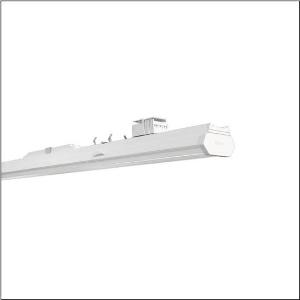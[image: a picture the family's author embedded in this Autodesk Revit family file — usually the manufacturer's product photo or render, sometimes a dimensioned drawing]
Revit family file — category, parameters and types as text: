
# Revit family: licross_r__21_protected_ho_52td12dn4e5md_1fe0
name_source: partatom
category: Lighting Fixtures
units: mm (PartAtom-declared; Revit-internal decimal feet)

## family parameters
Cut with Voids When Loaded = No
Host = Face
Light Source = No
Part Type = Normal
Room Calculation Point = No
Round Connector Dimension = Use Diameter
Shared = No

## types (1)
- --- (1 x LED, 2200 lm, 14.2 W, 4000K)
    Apparent Load = 14 VA
    CIE Flux Codes = 70 91 97 98 100
    Color Rendering = 80
    Color Temperature = 4000K
    Default Elevation = 1800 mm
    Description = Licross® 21 Protected HO, luminaire insert, of sheet steel, galvanised, coil coated, white, length: 1.500mm, width: 90mm, height: 103mm, LED rated luminous flux: 14.690lm, light colour: 840, control gear: DALI 2 (for two DALI lines), with plug, 6-pole, with phase selection, mains connection: 220..240V, AC/DC, 0/50..60Hz, rated input power: 85W, without changeover relay, for emergency light function, for central battery installations according to DIN EN 60598-2-22, halogen-free wiring, primary light control with lens, of plastic, primary optical cover: cover, of PMMA, light emission: direct distribution, primary light characteristic: symmetric, protection rating (complete): IP54, insulation class (complete): insulation class I (protective earthing), certification: CE, ENEC, VDE, UKCA, protection symbol: D if used in an environment with non-conductive dust loads with corresponding accessories, impact resistance: IK06, permissible ambient temperature for indoor applications: -25..+35°C, standard: EN 60598-2-22, corresponds to IFS (International Featured Standards) requirements for safety and quality in the food industry, reducing of maximum allowable ambient temperature of 5°C with ceiling mounting, LABS conformity tested according to VDMA 24364:2018-05, packaging unit: 1 piece
    Height = 92 mm
    Lamp = 1 x LED
    Lamp Light Flux = 2200 lm
    Lamp Power = 14.2 W
    Lamp count = 1
    Length = 1500 mm
    Luminous efficacy = 155 lm/W
    Manufacturer = Siteco
    ModVariant = No
    Model = 52TD12DN4E5MD
    Mounting Place = Ceiling
    Mounting Type = Pendant
    Number of Poles = 1
    OnlyDefault = Yes
    Power Factor = 1
    Product Name = Licross® 21 Protected HO
    Product group = luminaire insert
    ProductGroupID = 901
    Protection Class = Protection class I
    Protection Degree = IP 54
    RLX_Detail_Level = 1
    RLX_Emergency_Light_Flux = 0 lm
    RLX_Emergency_Type = 0
    RLX_Emergency_Type_DB = No
    RlxData = <blob elided: 24897 chars, md5=dd1ae46d>
    Socket = socket
    Standby Power = 0 W
    System Light Flux = 2200 lm
    System Power = 14 W
    Type Comments = : DC mode (central or group accumulator) initial emergency light level
    Type Image = l_1256148.jpg
    URL = http://relux.com
    VarID = @adj_085195
    Voltage = 0 V
    Weight = 0.00 kg
    Width = 88 mm

## geometry (parser evidence)
native form markers: Blend x4, Sweep x10
no freeform markers — native parametric forms only
